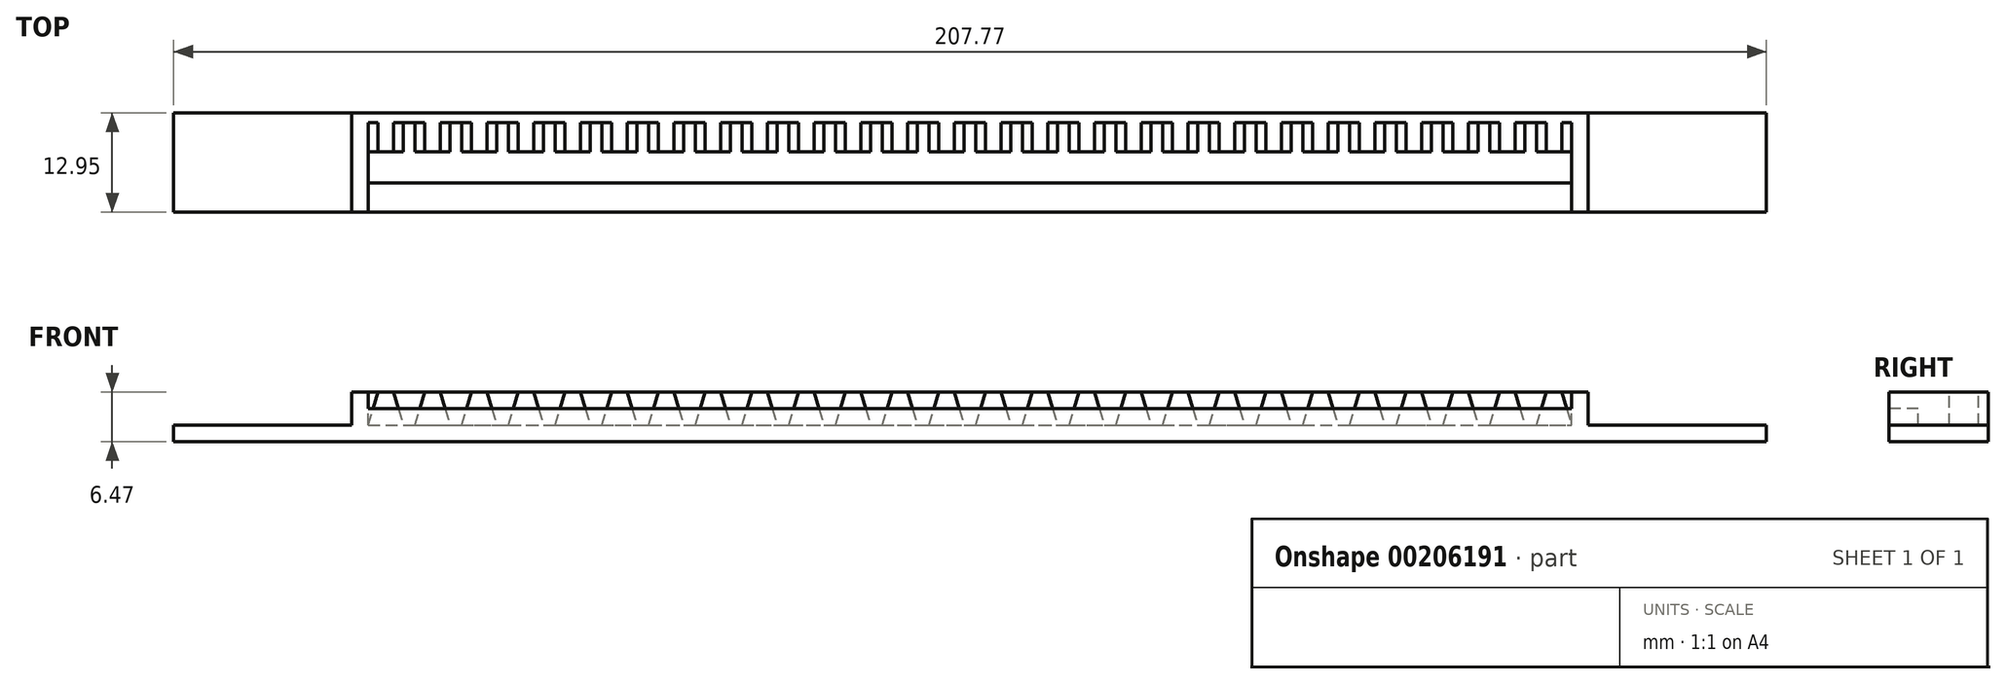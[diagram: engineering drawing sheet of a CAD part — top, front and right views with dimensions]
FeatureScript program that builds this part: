
annotation { "Feature Type Name" : "Feature", "Feature Type Description" : "" }
export const myFeature = defineFeature(function(context is Context, id is Id, definition is map)
    precondition{}
    {
        {
            var Q0;
            Q0=qCreatedBy(makeId("Front.planeOp"),FACE);
            var sketch = newSketch(context, id + "F0", { "sketchPlane" : qUnion([Q0])});
            skLineSegment(sketch, "E0.top", {"start": v(-38.44, 16.9) * mm, "end": v(33.18, 16.9) * mm});
            skLineSegment(sketch, "E0.left", {"start": v(-38.44, 14.74) * mm, "end": v(-38.44, 16.9) * mm});
            skLineSegment(sketch, "E1", {"start": v(-38.44, 16.9) * mm, "end": v(-37.17, 21.21) * mm});
            skLineSegment(sketch, "E2", {"start": v(-37.17, 21.21) * mm, "end": v(-35.14, 21.21) * mm});
            skLineSegment(sketch, "E3", {"start": v(-35.14, 21.21) * mm, "end": v(-33.87, 16.9) * mm});
            skLineSegment(sketch, "E4", {"start": v(-38.44, 16.9) * mm, "end": v(-33.87, 16.9) * mm});
            skLineSegment(sketch, "E5", {"start": v(-36.16, 21.21) * mm, "end": v(-36.16, 16.9) * mm, "construction": true});
            skLineSegment(sketch, "E6.1.0.0", {"start": v(-29.05, 21.21) * mm, "end": v(-27.78, 16.9) * mm});
            skLineSegment(sketch, "E6.1.0.1", {"start": v(-32.35, 16.9) * mm, "end": v(-31.08, 21.21) * mm});
            skLineSegment(sketch, "E6.1.0.2", {"start": v(-31.08, 21.21) * mm, "end": v(-29.05, 21.21) * mm});
            skLineSegment(sketch, "E6.2.0.0", {"start": v(-22.95, 21.21) * mm, "end": v(-21.68, 16.9) * mm});
            skLineSegment(sketch, "E6.2.0.1", {"start": v(-26.25, 16.9) * mm, "end": v(-24.98, 21.21) * mm});
            skLineSegment(sketch, "E6.2.0.2", {"start": v(-24.98, 21.21) * mm, "end": v(-22.95, 21.21) * mm});
            skLineSegment(sketch, "E6.3.0.0", {"start": v(-16.85, 21.21) * mm, "end": v(-15.58, 16.9) * mm});
            skLineSegment(sketch, "E6.3.0.1", {"start": v(-20.16, 16.9) * mm, "end": v(-18.89, 21.21) * mm});
            skLineSegment(sketch, "E6.3.0.2", {"start": v(-18.89, 21.21) * mm, "end": v(-16.85, 21.21) * mm});
            skLineSegment(sketch, "E6.4.0.0", {"start": v(-10.76, 21.21) * mm, "end": v(-9.49, 16.9) * mm});
            skLineSegment(sketch, "E6.4.0.1", {"start": v(-14.06, 16.9) * mm, "end": v(-12.8, 21.21) * mm});
            skLineSegment(sketch, "E6.4.0.2", {"start": v(-12.8, 21.21) * mm, "end": v(-10.76, 21.21) * mm});
            skLineSegment(sketch, "E6.5.0.0", {"start": v(-4.66, 21.21) * mm, "end": v(-3.4, 16.9) * mm});
            skLineSegment(sketch, "E6.5.0.1", {"start": v(-7.96, 16.9) * mm, "end": v(-6.7, 21.21) * mm});
            skLineSegment(sketch, "E6.5.0.2", {"start": v(-6.7, 21.21) * mm, "end": v(-4.66, 21.21) * mm});
            skLineSegment(sketch, "E6.6.0.0", {"start": v(1.43, 21.21) * mm, "end": v(2.7, 16.9) * mm});
            skLineSegment(sketch, "E6.6.0.1", {"start": v(-1.87, 16.9) * mm, "end": v(-0.6, 21.21) * mm});
            skLineSegment(sketch, "E6.6.0.2", {"start": v(-0.6, 21.21) * mm, "end": v(1.43, 21.21) * mm});
            skLineSegment(sketch, "E6.7.0.0", {"start": v(7.53, 21.21) * mm, "end": v(8.8, 16.9) * mm});
            skLineSegment(sketch, "E6.7.0.1", {"start": v(4.23, 16.9) * mm, "end": v(5.5, 21.21) * mm});
            skLineSegment(sketch, "E6.7.0.2", {"start": v(5.5, 21.21) * mm, "end": v(7.53, 21.21) * mm});
            skLineSegment(sketch, "E6.8.0.0", {"start": v(13.63, 21.21) * mm, "end": v(14.9, 16.9) * mm});
            skLineSegment(sketch, "E6.8.0.1", {"start": v(10.32, 16.9) * mm, "end": v(11.6, 21.21) * mm});
            skLineSegment(sketch, "E6.8.0.2", {"start": v(11.6, 21.21) * mm, "end": v(13.63, 21.21) * mm});
            skLineSegment(sketch, "E6.9.0.0", {"start": v(19.72, 21.21) * mm, "end": v(21, 16.9) * mm});
            skLineSegment(sketch, "E6.9.0.1", {"start": v(16.42, 16.9) * mm, "end": v(17.69, 21.21) * mm});
            skLineSegment(sketch, "E6.9.0.2", {"start": v(17.69, 21.21) * mm, "end": v(19.72, 21.21) * mm});
            skLineSegment(sketch, "E6.10.0.0", {"start": v(25.82, 21.21) * mm, "end": v(27.09, 16.9) * mm});
            skLineSegment(sketch, "E6.10.0.1", {"start": v(22.52, 16.9) * mm, "end": v(23.79, 21.21) * mm});
            skLineSegment(sketch, "E6.10.0.2", {"start": v(23.79, 21.21) * mm, "end": v(25.82, 21.21) * mm});
            skLineSegment(sketch, "E6.11.0.0", {"start": v(31.91, 21.21) * mm, "end": v(33.18, 16.9) * mm});
            skLineSegment(sketch, "E6.11.0.1", {"start": v(28.61, 16.9) * mm, "end": v(29.88, 21.21) * mm});
            skLineSegment(sketch, "E6.11.0.2", {"start": v(29.88, 21.21) * mm, "end": v(31.91, 21.21) * mm});
            skLineSegment(sketch, "E6.direction1", {"start": v(-38.44, 16.9) * mm, "end": v(-32.35, 16.9) * mm, "construction": true});
            skPoint(sketch, "E7.centerSnap0", {"position": v(-38.44, 15.82) * mm});
            skLineSegment(sketch, "E8.0.12.0", {"start": v(38, 21.21) * mm, "end": v(39.28, 16.9) * mm});
            skLineSegment(sketch, "E8.3.12.0", {"start": v(34.7, 16.9) * mm, "end": v(35.98, 21.21) * mm});
            skLineSegment(sketch, "E8.6.12.0", {"start": v(35.98, 21.21) * mm, "end": v(38, 21.21) * mm});
            skLineSegment(sketch, "E8.0.13.0", {"start": v(44.1, 21.21) * mm, "end": v(45.38, 16.9) * mm});
            skLineSegment(sketch, "E8.3.13.0", {"start": v(40.8, 16.9) * mm, "end": v(42.07, 21.21) * mm});
            skLineSegment(sketch, "E8.6.13.0", {"start": v(42.07, 21.21) * mm, "end": v(44.1, 21.21) * mm});
            skLineSegment(sketch, "E8.0.14.0", {"start": v(50.2, 21.21) * mm, "end": v(51.47, 16.9) * mm});
            skLineSegment(sketch, "E8.3.14.0", {"start": v(46.9, 16.9) * mm, "end": v(48.17, 21.21) * mm});
            skLineSegment(sketch, "E8.6.14.0", {"start": v(48.17, 21.21) * mm, "end": v(50.2, 21.21) * mm});
            skLineSegment(sketch, "E8.0.15.0", {"start": v(56.3, 21.21) * mm, "end": v(57.57, 16.9) * mm});
            skLineSegment(sketch, "E8.3.15.0", {"start": v(53, 16.9) * mm, "end": v(54.27, 21.21) * mm});
            skLineSegment(sketch, "E8.6.15.0", {"start": v(54.27, 21.21) * mm, "end": v(56.3, 21.21) * mm});
            skLineSegment(sketch, "E8.0.16.0", {"start": v(62.4, 21.21) * mm, "end": v(63.66, 16.9) * mm});
            skLineSegment(sketch, "E8.3.16.0", {"start": v(59.1, 16.9) * mm, "end": v(60.36, 21.21) * mm});
            skLineSegment(sketch, "E8.6.16.0", {"start": v(60.36, 21.21) * mm, "end": v(62.4, 21.21) * mm});
            skLineSegment(sketch, "E8.0.17.0", {"start": v(68.49, 21.21) * mm, "end": v(69.76, 16.9) * mm});
            skLineSegment(sketch, "E8.3.17.0", {"start": v(65.19, 16.9) * mm, "end": v(66.46, 21.21) * mm});
            skLineSegment(sketch, "E8.6.17.0", {"start": v(66.46, 21.21) * mm, "end": v(68.49, 21.21) * mm});
            skLineSegment(sketch, "E9.0.18.0", {"start": v(74.59, 21.21) * mm, "end": v(75.86, 16.9) * mm});
            skLineSegment(sketch, "E9.3.18.0", {"start": v(71.28, 16.9) * mm, "end": v(72.55, 21.21) * mm});
            skLineSegment(sketch, "E9.6.18.0", {"start": v(72.55, 21.21) * mm, "end": v(74.59, 21.21) * mm});
            skLineSegment(sketch, "E9.0.19.0", {"start": v(80.68, 21.21) * mm, "end": v(81.95, 16.9) * mm});
            skLineSegment(sketch, "E9.3.19.0", {"start": v(77.38, 16.9) * mm, "end": v(78.65, 21.21) * mm});
            skLineSegment(sketch, "E9.6.19.0", {"start": v(78.65, 21.21) * mm, "end": v(80.68, 21.21) * mm});
            skLineSegment(sketch, "E10.0.20.0", {"start": v(86.78, 21.21) * mm, "end": v(88.05, 16.9) * mm});
            skLineSegment(sketch, "E10.3.20.0", {"start": v(83.48, 16.9) * mm, "end": v(84.75, 21.21) * mm});
            skLineSegment(sketch, "E10.6.20.0", {"start": v(84.75, 21.21) * mm, "end": v(86.78, 21.21) * mm});
            skLineSegment(sketch, "E10.0.21.0", {"start": v(92.87, 21.21) * mm, "end": v(94.14, 16.9) * mm});
            skLineSegment(sketch, "E10.3.21.0", {"start": v(89.57, 16.9) * mm, "end": v(90.84, 21.21) * mm});
            skLineSegment(sketch, "E10.6.21.0", {"start": v(90.84, 21.21) * mm, "end": v(92.87, 21.21) * mm});
            skLineSegment(sketch, "E10.0.22.0", {"start": v(98.97, 21.21) * mm, "end": v(100.24, 16.9) * mm});
            skLineSegment(sketch, "E10.3.22.0", {"start": v(95.67, 16.9) * mm, "end": v(96.94, 21.21) * mm});
            skLineSegment(sketch, "E10.6.22.0", {"start": v(96.94, 21.21) * mm, "end": v(98.97, 21.21) * mm});
            skLineSegment(sketch, "E10.0.23.0", {"start": v(105.07, 21.21) * mm, "end": v(106.34, 16.9) * mm});
            skLineSegment(sketch, "E10.3.23.0", {"start": v(101.76, 16.9) * mm, "end": v(103.03, 21.21) * mm});
            skLineSegment(sketch, "E10.6.23.0", {"start": v(103.03, 21.21) * mm, "end": v(105.07, 21.21) * mm});
            skLineSegment(sketch, "E11.0.24.0", {"start": v(111.16, 21.21) * mm, "end": v(112.43, 16.9) * mm});
            skLineSegment(sketch, "E11.3.24.0", {"start": v(107.86, 16.9) * mm, "end": v(109.13, 21.21) * mm});
            skLineSegment(sketch, "E11.6.24.0", {"start": v(109.13, 21.21) * mm, "end": v(111.16, 21.21) * mm});
            skLineSegment(sketch, "E12.0.25.0", {"start": v(117.26, 21.21) * mm, "end": v(118.53, 16.9) * mm});
            skLineSegment(sketch, "E12.3.25.0", {"start": v(113.96, 16.9) * mm, "end": v(115.23, 21.21) * mm});
            skLineSegment(sketch, "E12.6.25.0", {"start": v(115.23, 21.21) * mm, "end": v(117.26, 21.21) * mm});
            skLineSegment(sketch, "E13", {"start": v(33.18, 16.9) * mm, "end": v(118.53, 16.9) * mm});
            skLineSegment(sketch, "E14", {"start": v(-38.44, 14.74) * mm, "end": v(118.53, 14.74) * mm});
            skLineSegment(sketch, "E15", {"start": v(118.53, 14.74) * mm, "end": v(118.53, 16.9) * mm});
            skSolve(sketch);
        }
        {
            var Q0;
            Q0=qSketchRegion(id+"F0",true);
            extrude(context, id + "F1", {"entities" : qUnion([Q0]), "depth" : 3.8 * mm});
        }
        {
            var Q0;
            Q0=makeQuery(id+"F1.opExtrude","SWEPT_EDGE",EDGE,{"disambiguationData":[OSD([sQuery(id+"F0.wireOp",EDGE,"E14"),sQuery(id+"F0.wireOp",EDGE,"E15")])]});
            cPoint(context, id + "F2", {"entities" : qUnion([Q0]), "parameter" : 0.5});
        }
        {
            var Q0;
            Q0=qCreatedBy(makeId("Right.planeOp"),FACE);
            var Q1;
            Q1=qCreatedBy(id+"F2",VERTEX);
            cPlane(context, id + "F3", {"entities" : qUnion([Q0, Q1]), "cplaneType" : CPlaneType.PLANE_POINT, "offset" : 25.4 * mm, "width" : 152.4 * mm, "height" : 152.4 * mm});
        }
        {
            var Q0;
            Q0=qCreatedBy(id+"F3.planeOp",FACE);
            var sketch = newSketch(context, id + "F4", { "sketchPlane" : qUnion([Q0])});
            skLineSegment(sketch, "E16.0", {"start": v(-3.81, 14.74) * mm, "end": v(-3.81, 16.9) * mm});
            skLineSegment(sketch, "E17", {"start": v(-15.5, 16.9) * mm, "end": v(-11.68, 16.9) * mm});
            skLineSegment(sketch, "E18", {"start": v(-7.87, 16.9) * mm, "end": v(-7.87, 19.05) * mm});
            skLineSegment(sketch, "E19", {"start": v(-7.87, 19.05) * mm, "end": v(-11.68, 19.05) * mm});
            skLineSegment(sketch, "E20", {"start": v(-11.68, 19.05) * mm, "end": v(-11.68, 16.9) * mm});
            skLineSegment(sketch, "E21.trimOffspring", {"start": v(-7.87, 16.9) * mm, "end": v(-3.81, 16.9) * mm});
            skLineSegment(sketch, "E22", {"start": v(-3.81, 14.74) * mm, "end": v(-15.5, 14.74) * mm});
            skLineSegment(sketch, "E23", {"start": v(-15.5, 14.74) * mm, "end": v(-15.5, 16.9) * mm});
            skLineSegment(sketch, "E24", {"start": v(-11.68, 16.9) * mm, "end": v(-11.68, 14.74) * mm});
            skSolve(sketch);
        }
        {
            var Q0;
            {var subQ0=sQuery(id+"F4.wireOp",EDGE,"E16.0");Q0=makeQuery(id+"F4.imprint","IMPRINT",FACE,{"disambiguationData":[TD([[makeQuery(id+"F4.imprint","IMPRINT",EDGE,{"derivedFrom":subQ0}),1.0]])]});}
            var Q1;
            Q1=makeQuery(id+"F1.opExtrude","SWEPT_FACE",FACE,{"disambiguationData":[OSD([sQuery(id+"F0.wireOp",EDGE,"E0.left")])]});
            extrude(context, id + "F5", {"entities" : qUnion([Q0]), "operationType" : NewBodyOperationType.ADD, "endBound" : BoundingType.UP_TO_SURFACE, "oppositeDirection" : true, "endBoundEntityFace" : qUnion([Q1]), "depth" : 33.02 * mm});
        }
        {
            var Q0;
            Q0=makeQuery(id+"F1.opExtrude","CAP_FACE",FACE,{"disambiguationData":[OSD([sQuery(id+"F0.wireOp",EDGE,"E0.bottom"),sQuery(id+"F0.wireOp",EDGE,"E0.top"),sQuery(id+"F0.wireOp",EDGE,"E0.left"),sQuery(id+"F0.wireOp",EDGE,"E1"),sQuery(id+"F0.wireOp",EDGE,"E2"),sQuery(id+"F0.wireOp",EDGE,"E3"),sQuery(id+"F0.wireOp",EDGE,"9qWjWlUo-ttb5-mKxR-HVll-tsb38tv3fsYN"),sQuery(id+"F0.wireOp",EDGE,"E6.1.0.0"),sQuery(id+"F0.wireOp",EDGE,"E6.1.0.1"),sQuery(id+"F0.wireOp",EDGE,"E6.1.0.2"),sQuery(id+"F0.wireOp",EDGE,"E6.2.0.0"),sQuery(id+"F0.wireOp",EDGE,"E6.2.0.1"),sQuery(id+"F0.wireOp",EDGE,"E6.2.0.2"),sQuery(id+"F0.wireOp",EDGE,"E6.3.0.0"),sQuery(id+"F0.wireOp",EDGE,"E6.3.0.1"),sQuery(id+"F0.wireOp",EDGE,"E6.3.0.2"),sQuery(id+"F0.wireOp",EDGE,"E6.4.0.0"),sQuery(id+"F0.wireOp",EDGE,"E6.4.0.1"),sQuery(id+"F0.wireOp",EDGE,"E6.4.0.2"),sQuery(id+"F0.wireOp",EDGE,"E6.5.0.0"),sQuery(id+"F0.wireOp",EDGE,"E6.5.0.1"),sQuery(id+"F0.wireOp",EDGE,"E6.5.0.2"),sQuery(id+"F0.wireOp",EDGE,"E6.6.0.0"),sQuery(id+"F0.wireOp",EDGE,"E6.6.0.1"),sQuery(id+"F0.wireOp",EDGE,"E6.6.0.2"),sQuery(id+"F0.wireOp",EDGE,"E6.7.0.0"),sQuery(id+"F0.wireOp",EDGE,"E6.7.0.1"),sQuery(id+"F0.wireOp",EDGE,"E6.7.0.2"),sQuery(id+"F0.wireOp",EDGE,"E6.8.0.0"),sQuery(id+"F0.wireOp",EDGE,"E6.8.0.1"),sQuery(id+"F0.wireOp",EDGE,"E6.8.0.2"),sQuery(id+"F0.wireOp",EDGE,"E6.9.0.0"),sQuery(id+"F0.wireOp",EDGE,"E6.9.0.1"),sQuery(id+"F0.wireOp",EDGE,"E6.9.0.2"),sQuery(id+"F0.wireOp",EDGE,"E6.10.0.0"),sQuery(id+"F0.wireOp",EDGE,"E6.10.0.1"),sQuery(id+"F0.wireOp",EDGE,"E6.10.0.2"),sQuery(id+"F0.wireOp",EDGE,"E6.11.0.0"),sQuery(id+"F0.wireOp",EDGE,"E6.11.0.1"),sQuery(id+"F0.wireOp",EDGE,"E6.11.0.2")])],"isStart":true});
            var sketch = newSketch(context, id + "F6", { "sketchPlane" : qUnion([Q0])});
            skPoint(sketch, "E25.oppositeSnap0", {"position": v(23.97, 21.21) * mm});
            skLineSegment(sketch, "E25.bottom", {"start": v(38.44, 14.74) * mm, "end": v(-118.53, 14.74) * mm});
            skLineSegment(sketch, "E25.top", {"start": v(38.44, 21.21) * mm, "end": v(-118.53, 21.21) * mm});
            skLineSegment(sketch, "E25.left", {"start": v(38.44, 14.74) * mm, "end": v(38.44, 21.21) * mm});
            skLineSegment(sketch, "E25.right", {"start": v(-118.53, 14.74) * mm, "end": v(-118.53, 21.21) * mm});
            skLineSegment(sketch, "E26.0", {"start": v(38.44, 16.9) * mm, "end": v(37.17, 21.21) * mm});
            skLineSegment(sketch, "E27.0", {"start": v(-117.26, 21.21) * mm, "end": v(-118.53, 16.9) * mm});
            skSolve(sketch);
        }
        {
            var Q0;
            {var subQ1=sQuery(id+"F0.wireOp",EDGE,"E3");var subQ2=makeQuery(id+"F1.opExtrude","CAP_EDGE",EDGE,{"disambiguationData":[OSD([subQ1])],"isStart":true});Q0=makeQuery(id+"F6.imprint","IMPRINT",FACE,{"disambiguationData":[TD([[makeQuery(id+"F6.imprint","IMPRINT",EDGE,{"derivedFrom":subQ2}),-1.0]])]});}
            var Q1;
            {var subQ1=sQuery(id+"F0.wireOp",EDGE,"E6.1.0.0");var subQ2=makeQuery(id+"F1.opExtrude","CAP_EDGE",EDGE,{"disambiguationData":[OSD([subQ1])],"isStart":true});Q1=makeQuery(id+"F6.imprint","IMPRINT",FACE,{"disambiguationData":[TD([[makeQuery(id+"F6.imprint","IMPRINT",EDGE,{"derivedFrom":subQ2}),-1.0]])]});}
            var Q2;
            {var subQ1=sQuery(id+"F0.wireOp",EDGE,"E6.2.0.0");var subQ2=makeQuery(id+"F1.opExtrude","CAP_EDGE",EDGE,{"disambiguationData":[OSD([subQ1])],"isStart":true});Q2=makeQuery(id+"F6.imprint","IMPRINT",FACE,{"disambiguationData":[TD([[makeQuery(id+"F6.imprint","IMPRINT",EDGE,{"derivedFrom":subQ2}),-1.0]])]});}
            var Q3;
            {var subQ1=sQuery(id+"F0.wireOp",EDGE,"E6.3.0.0");var subQ2=makeQuery(id+"F1.opExtrude","CAP_EDGE",EDGE,{"disambiguationData":[OSD([subQ1])],"isStart":true});Q3=makeQuery(id+"F6.imprint","IMPRINT",FACE,{"disambiguationData":[TD([[makeQuery(id+"F6.imprint","IMPRINT",EDGE,{"derivedFrom":subQ2}),-1.0]])]});}
            var Q4;
            {var subQ1=sQuery(id+"F0.wireOp",EDGE,"E6.4.0.0");var subQ2=makeQuery(id+"F1.opExtrude","CAP_EDGE",EDGE,{"disambiguationData":[OSD([subQ1])],"isStart":true});Q4=makeQuery(id+"F6.imprint","IMPRINT",FACE,{"disambiguationData":[TD([[makeQuery(id+"F6.imprint","IMPRINT",EDGE,{"derivedFrom":subQ2}),-1.0]])]});}
            var Q5;
            {var subQ1=sQuery(id+"F0.wireOp",EDGE,"E6.5.0.0");var subQ2=makeQuery(id+"F1.opExtrude","CAP_EDGE",EDGE,{"disambiguationData":[OSD([subQ1])],"isStart":true});Q5=makeQuery(id+"F6.imprint","IMPRINT",FACE,{"disambiguationData":[TD([[makeQuery(id+"F6.imprint","IMPRINT",EDGE,{"derivedFrom":subQ2}),-1.0]])]});}
            var Q6;
            {var subQ1=sQuery(id+"F0.wireOp",EDGE,"E6.6.0.0");var subQ2=makeQuery(id+"F1.opExtrude","CAP_EDGE",EDGE,{"disambiguationData":[OSD([subQ1])],"isStart":true});Q6=makeQuery(id+"F6.imprint","IMPRINT",FACE,{"disambiguationData":[TD([[makeQuery(id+"F6.imprint","IMPRINT",EDGE,{"derivedFrom":subQ2}),-1.0]])]});}
            var Q7;
            {var subQ1=sQuery(id+"F0.wireOp",EDGE,"E6.7.0.0");var subQ2=makeQuery(id+"F1.opExtrude","CAP_EDGE",EDGE,{"disambiguationData":[OSD([subQ1])],"isStart":true});Q7=makeQuery(id+"F6.imprint","IMPRINT",FACE,{"disambiguationData":[TD([[makeQuery(id+"F6.imprint","IMPRINT",EDGE,{"derivedFrom":subQ2}),-1.0]])]});}
            var Q8;
            {var subQ1=sQuery(id+"F0.wireOp",EDGE,"E6.8.0.0");var subQ2=makeQuery(id+"F1.opExtrude","CAP_EDGE",EDGE,{"disambiguationData":[OSD([subQ1])],"isStart":true});Q8=makeQuery(id+"F6.imprint","IMPRINT",FACE,{"disambiguationData":[TD([[makeQuery(id+"F6.imprint","IMPRINT",EDGE,{"derivedFrom":subQ2}),-1.0]])]});}
            var Q9;
            {var subQ1=sQuery(id+"F0.wireOp",EDGE,"E6.9.0.0");var subQ2=makeQuery(id+"F1.opExtrude","CAP_EDGE",EDGE,{"disambiguationData":[OSD([subQ1])],"isStart":true});Q9=makeQuery(id+"F6.imprint","IMPRINT",FACE,{"disambiguationData":[TD([[makeQuery(id+"F6.imprint","IMPRINT",EDGE,{"derivedFrom":subQ2}),-1.0]])]});}
            var Q10;
            {var subQ1=sQuery(id+"F0.wireOp",EDGE,"E6.10.0.0");var subQ2=makeQuery(id+"F1.opExtrude","CAP_EDGE",EDGE,{"disambiguationData":[OSD([subQ1])],"isStart":true});Q10=makeQuery(id+"F6.imprint","IMPRINT",FACE,{"disambiguationData":[TD([[makeQuery(id+"F6.imprint","IMPRINT",EDGE,{"derivedFrom":subQ2}),-1.0]])]});}
            var Q11;
            {var subQ42=sQuery(id+"F6.wireOp",EDGE,"E25.bottom");Q11=makeQuery(id+"F6.imprint","IMPRINT",FACE,{"disambiguationData":[TD([[makeQuery(id+"F6.imprint","IMPRINT",EDGE,{"derivedFrom":subQ42}),-1.0]])]});}
            var Q12;
            {var subQ1=sQuery(id+"F0.wireOp",EDGE,"E11.0.24.0");var subQ2=makeQuery(id+"F1.opExtrude","CAP_EDGE",EDGE,{"disambiguationData":[OSD([subQ1])],"isStart":true});Q12=makeQuery(id+"F6.imprint","IMPRINT",FACE,{"disambiguationData":[TD([[makeQuery(id+"F6.imprint","IMPRINT",EDGE,{"derivedFrom":subQ2}),-1.0]])]});}
            var Q13;
            {var subQ1=sQuery(id+"F0.wireOp",EDGE,"E10.0.23.0");var subQ2=makeQuery(id+"F1.opExtrude","CAP_EDGE",EDGE,{"disambiguationData":[OSD([subQ1])],"isStart":true});Q13=makeQuery(id+"F6.imprint","IMPRINT",FACE,{"disambiguationData":[TD([[makeQuery(id+"F6.imprint","IMPRINT",EDGE,{"derivedFrom":subQ2}),-1.0]])]});}
            var Q14;
            {var subQ1=sQuery(id+"F0.wireOp",EDGE,"E10.0.22.0");var subQ2=makeQuery(id+"F1.opExtrude","CAP_EDGE",EDGE,{"disambiguationData":[OSD([subQ1])],"isStart":true});Q14=makeQuery(id+"F6.imprint","IMPRINT",FACE,{"disambiguationData":[TD([[makeQuery(id+"F6.imprint","IMPRINT",EDGE,{"derivedFrom":subQ2}),-1.0]])]});}
            var Q15;
            {var subQ1=sQuery(id+"F0.wireOp",EDGE,"E10.0.21.0");var subQ2=makeQuery(id+"F1.opExtrude","CAP_EDGE",EDGE,{"disambiguationData":[OSD([subQ1])],"isStart":true});Q15=makeQuery(id+"F6.imprint","IMPRINT",FACE,{"disambiguationData":[TD([[makeQuery(id+"F6.imprint","IMPRINT",EDGE,{"derivedFrom":subQ2}),-1.0]])]});}
            var Q16;
            {var subQ1=sQuery(id+"F0.wireOp",EDGE,"E10.0.20.0");var subQ2=makeQuery(id+"F1.opExtrude","CAP_EDGE",EDGE,{"disambiguationData":[OSD([subQ1])],"isStart":true});Q16=makeQuery(id+"F6.imprint","IMPRINT",FACE,{"disambiguationData":[TD([[makeQuery(id+"F6.imprint","IMPRINT",EDGE,{"derivedFrom":subQ2}),-1.0]])]});}
            var Q17;
            {var subQ1=sQuery(id+"F0.wireOp",EDGE,"E9.0.19.0");var subQ2=makeQuery(id+"F1.opExtrude","CAP_EDGE",EDGE,{"disambiguationData":[OSD([subQ1])],"isStart":true});Q17=makeQuery(id+"F6.imprint","IMPRINT",FACE,{"disambiguationData":[TD([[makeQuery(id+"F6.imprint","IMPRINT",EDGE,{"derivedFrom":subQ2}),-1.0]])]});}
            var Q18;
            {var subQ1=sQuery(id+"F0.wireOp",EDGE,"E9.0.18.0");var subQ2=makeQuery(id+"F1.opExtrude","CAP_EDGE",EDGE,{"disambiguationData":[OSD([subQ1])],"isStart":true});Q18=makeQuery(id+"F6.imprint","IMPRINT",FACE,{"disambiguationData":[TD([[makeQuery(id+"F6.imprint","IMPRINT",EDGE,{"derivedFrom":subQ2}),-1.0]])]});}
            var Q19;
            {var subQ1=sQuery(id+"F0.wireOp",EDGE,"E8.0.17.0");var subQ2=makeQuery(id+"F1.opExtrude","CAP_EDGE",EDGE,{"disambiguationData":[OSD([subQ1])],"isStart":true});Q19=makeQuery(id+"F6.imprint","IMPRINT",FACE,{"disambiguationData":[TD([[makeQuery(id+"F6.imprint","IMPRINT",EDGE,{"derivedFrom":subQ2}),-1.0]])]});}
            var Q20;
            {var subQ1=sQuery(id+"F0.wireOp",EDGE,"E8.0.16.0");var subQ2=makeQuery(id+"F1.opExtrude","CAP_EDGE",EDGE,{"disambiguationData":[OSD([subQ1])],"isStart":true});Q20=makeQuery(id+"F6.imprint","IMPRINT",FACE,{"disambiguationData":[TD([[makeQuery(id+"F6.imprint","IMPRINT",EDGE,{"derivedFrom":subQ2}),-1.0]])]});}
            var Q21;
            {var subQ1=sQuery(id+"F0.wireOp",EDGE,"E8.0.15.0");var subQ2=makeQuery(id+"F1.opExtrude","CAP_EDGE",EDGE,{"disambiguationData":[OSD([subQ1])],"isStart":true});Q21=makeQuery(id+"F6.imprint","IMPRINT",FACE,{"disambiguationData":[TD([[makeQuery(id+"F6.imprint","IMPRINT",EDGE,{"derivedFrom":subQ2}),-1.0]])]});}
            var Q22;
            {var subQ1=sQuery(id+"F0.wireOp",EDGE,"E8.0.14.0");var subQ2=makeQuery(id+"F1.opExtrude","CAP_EDGE",EDGE,{"disambiguationData":[OSD([subQ1])],"isStart":true});Q22=makeQuery(id+"F6.imprint","IMPRINT",FACE,{"disambiguationData":[TD([[makeQuery(id+"F6.imprint","IMPRINT",EDGE,{"derivedFrom":subQ2}),-1.0]])]});}
            var Q23;
            {var subQ1=sQuery(id+"F0.wireOp",EDGE,"E8.0.13.0");var subQ2=makeQuery(id+"F1.opExtrude","CAP_EDGE",EDGE,{"disambiguationData":[OSD([subQ1])],"isStart":true});Q23=makeQuery(id+"F6.imprint","IMPRINT",FACE,{"disambiguationData":[TD([[makeQuery(id+"F6.imprint","IMPRINT",EDGE,{"derivedFrom":subQ2}),-1.0]])]});}
            var Q24;
            {var subQ1=sQuery(id+"F0.wireOp",EDGE,"E8.0.12.0");var subQ2=makeQuery(id+"F1.opExtrude","CAP_EDGE",EDGE,{"disambiguationData":[OSD([subQ1])],"isStart":true});Q24=makeQuery(id+"F6.imprint","IMPRINT",FACE,{"disambiguationData":[TD([[makeQuery(id+"F6.imprint","IMPRINT",EDGE,{"derivedFrom":subQ2}),-1.0]])]});}
            var Q25;
            {var subQ1=sQuery(id+"F0.wireOp",EDGE,"E6.11.0.0");var subQ2=makeQuery(id+"F1.opExtrude","CAP_EDGE",EDGE,{"disambiguationData":[OSD([subQ1])],"isStart":true});Q25=makeQuery(id+"F6.imprint","IMPRINT",FACE,{"disambiguationData":[TD([[makeQuery(id+"F6.imprint","IMPRINT",EDGE,{"derivedFrom":subQ2}),-1.0]])]});}
            var Q26;
            {var subQ0=sQuery(id+"F6.wireOp",EDGE,"E27.0");Q26=makeQuery(id+"F6.imprint","IMPRINT",FACE,{"disambiguationData":[TD([[makeQuery(id+"F6.imprint","IMPRINT",EDGE,{"derivedFrom":subQ0}),-1.0]])]});}
            var Q27;
            {var subQ0=sQuery(id+"F6.wireOp",EDGE,"E26.0");Q27=makeQuery(id+"F6.imprint","IMPRINT",FACE,{"disambiguationData":[TD([[makeQuery(id+"F6.imprint","IMPRINT",EDGE,{"derivedFrom":subQ0}),-1.0]])]});}
            extrude(context, id + "F7", {"entities" : qUnion([Q0, Q1, Q2, Q3, Q4, Q5, Q6, Q7, Q8, Q9, Q10, Q11, Q12, Q13, Q14, Q15, Q16, Q17, Q18, Q19, Q20, Q21, Q22, Q23, Q24, Q25, Q26, Q27]), "operationType" : NewBodyOperationType.ADD, "depth" : 1.27 * mm});
        }
        {
            var Q0;
            Q0=makeQuery(id+"F7.boolean.opBoolean","MERGE",FACE,{"derivedFrom":[makeQuery(id+"F5.boolean.opBoolean","MERGE",FACE,{"derivedFrom":[makeQuery(id+"F1.opExtrude","SWEPT_FACE",FACE,{"disambiguationData":[OSD([sQuery(id+"F0.wireOp",EDGE,"E15")])]}),makeQuery(id+"F5.opExtrude","CAP_FACE",FACE,{"disambiguationData":[OSD([sQuery(id+"F4.wireOp",EDGE,"E16.0"),sQuery(id+"F4.wireOp",EDGE,"E18"),sQuery(id+"F4.wireOp",EDGE,"E19"),sQuery(id+"F4.wireOp",EDGE,"E20"),sQuery(id+"F4.wireOp",EDGE,"E21.trimOffspring"),sQuery(id+"F4.wireOp",EDGE,"E22"),sQuery(id+"F4.wireOp",EDGE,"E24")])],"isStart":true})]}),makeQuery(id+"F7.opExtrude","SWEPT_FACE",FACE,{"disambiguationData":[OSD([sQuery(id+"F6.wireOp",EDGE,"E25.right")])]})]});
            var sketch = newSketch(context, id + "F9", { "sketchPlane" : qUnion([Q0])});
            skLineSegment(sketch, "E28.bottom", {"start": v(-11.68, 14.74) * mm, "end": v(1.27, 14.74) * mm});
            skLineSegment(sketch, "E28.top", {"start": v(-11.68, 21.21) * mm, "end": v(1.27, 21.21) * mm});
            skLineSegment(sketch, "E28.left", {"start": v(-11.68, 14.74) * mm, "end": v(-11.68, 21.21) * mm});
            skLineSegment(sketch, "E28.right", {"start": v(1.27, 14.74) * mm, "end": v(1.27, 21.21) * mm});
            skLineSegment(sketch, "E29.top", {"start": v(-11.68, 16.9) * mm, "end": v(1.27, 16.9) * mm});
            skLineSegment(sketch, "E29.left", {"start": v(-11.68, 14.74) * mm, "end": v(-11.68, 16.9) * mm});
            skLineSegment(sketch, "E29.right", {"start": v(1.27, 14.74) * mm, "end": v(1.27, 16.9) * mm});
            skSolve(sketch);
        }
        {
            var Q0;
            Q0=qSketchRegion(id+"F9",true);
            extrude(context, id + "F10", {"entities" : qUnion([Q0]), "operationType" : NewBodyOperationType.ADD, "depth" : 2.16 * mm});
        }
        {
            var Q0;
            Q0=makeQuery(id+"F9.imprint","IMPRINT",FACE,{"disambiguationData":[TD([[makeQuery(id+"F9.imprint","IMPRINT",EDGE,{"derivedFrom":sQuery(id+"F9.wireOp",EDGE,"E28.bottom")}),1.0]])]});
            extrude(context, id + "F11", {"entities" : qUnion([Q0]), "operationType" : NewBodyOperationType.ADD, "depth" : 25.4 * mm});
        }
        {
            var Q0;
            {var subQ0=sQuery(id+"F0.wireOp",EDGE,"E0.left");Q0=makeQuery(id+"F7.boolean.opBoolean","MERGE",FACE,{"derivedFrom":[makeQuery(id+"F5.boolean.opBoolean","MERGE",FACE,{"derivedFrom":[makeQuery(id+"F1.opExtrude","SWEPT_FACE",FACE,{"disambiguationData":[OSD([subQ0])]}),makeQuery(id+"F5.opExtrude","CAP_FACE",FACE,{"disambiguationData":[OSD([subQ0])],"isStart":false})]}),makeQuery(id+"F7.opExtrude","SWEPT_FACE",FACE,{"disambiguationData":[OSD([sQuery(id+"F6.wireOp",EDGE,"E25.left")])]})]});}
            var sketch = newSketch(context, id + "F12", { "sketchPlane" : qUnion([Q0])});
            skLineSegment(sketch, "E30.0", {"start": v(11.68, 21.21) * mm, "end": v(-1.27, 21.21) * mm});
            skLineSegment(sketch, "E31.bottom", {"start": v(11.68, 14.74) * mm, "end": v(-1.27, 14.74) * mm});
            skLineSegment(sketch, "E31.left", {"start": v(11.68, 14.74) * mm, "end": v(11.68, 21.21) * mm});
            skLineSegment(sketch, "E31.right", {"start": v(-1.27, 14.74) * mm, "end": v(-1.27, 21.21) * mm});
            skLineSegment(sketch, "E32.left", {"start": v(11.68, 14.74) * mm, "end": v(11.68, 14.74) * mm});
            skLineSegment(sketch, "E32.right", {"start": v(-1.27, 14.74) * mm, "end": v(-1.27, 14.74) * mm});
            skPoint(sketch, "E33.oppositeSnap0", {"position": v(-1.27, 17.97) * mm});
            skLineSegment(sketch, "E33.top", {"start": v(11.68, 16.9) * mm, "end": v(-1.27, 16.9) * mm});
            skLineSegment(sketch, "E33.left", {"start": v(11.68, 14.74) * mm, "end": v(11.68, 16.9) * mm});
            skLineSegment(sketch, "E33.right", {"start": v(-1.27, 14.74) * mm, "end": v(-1.27, 16.9) * mm});
            skSolve(sketch);
        }
        {
            var Q0;
            Q0=qSketchRegion(id+"F12",true);
            extrude(context, id + "F13", {"entities" : qUnion([Q0]), "operationType" : NewBodyOperationType.ADD, "depth" : 2.16 * mm});
        }
        {
            var Q0;
            Q0=makeQuery(id+"F12.imprint","IMPRINT",FACE,{"disambiguationData":[TD([[makeQuery(id+"F12.imprint","IMPRINT",EDGE,{"derivedFrom":sQuery(id+"F12.wireOp",EDGE,"E31.bottom")}),-1.0]])]});
            extrude(context, id + "F14", {"entities" : qUnion([Q0]), "operationType" : NewBodyOperationType.ADD, "depth" : 25.4 * mm});
        }
    });
